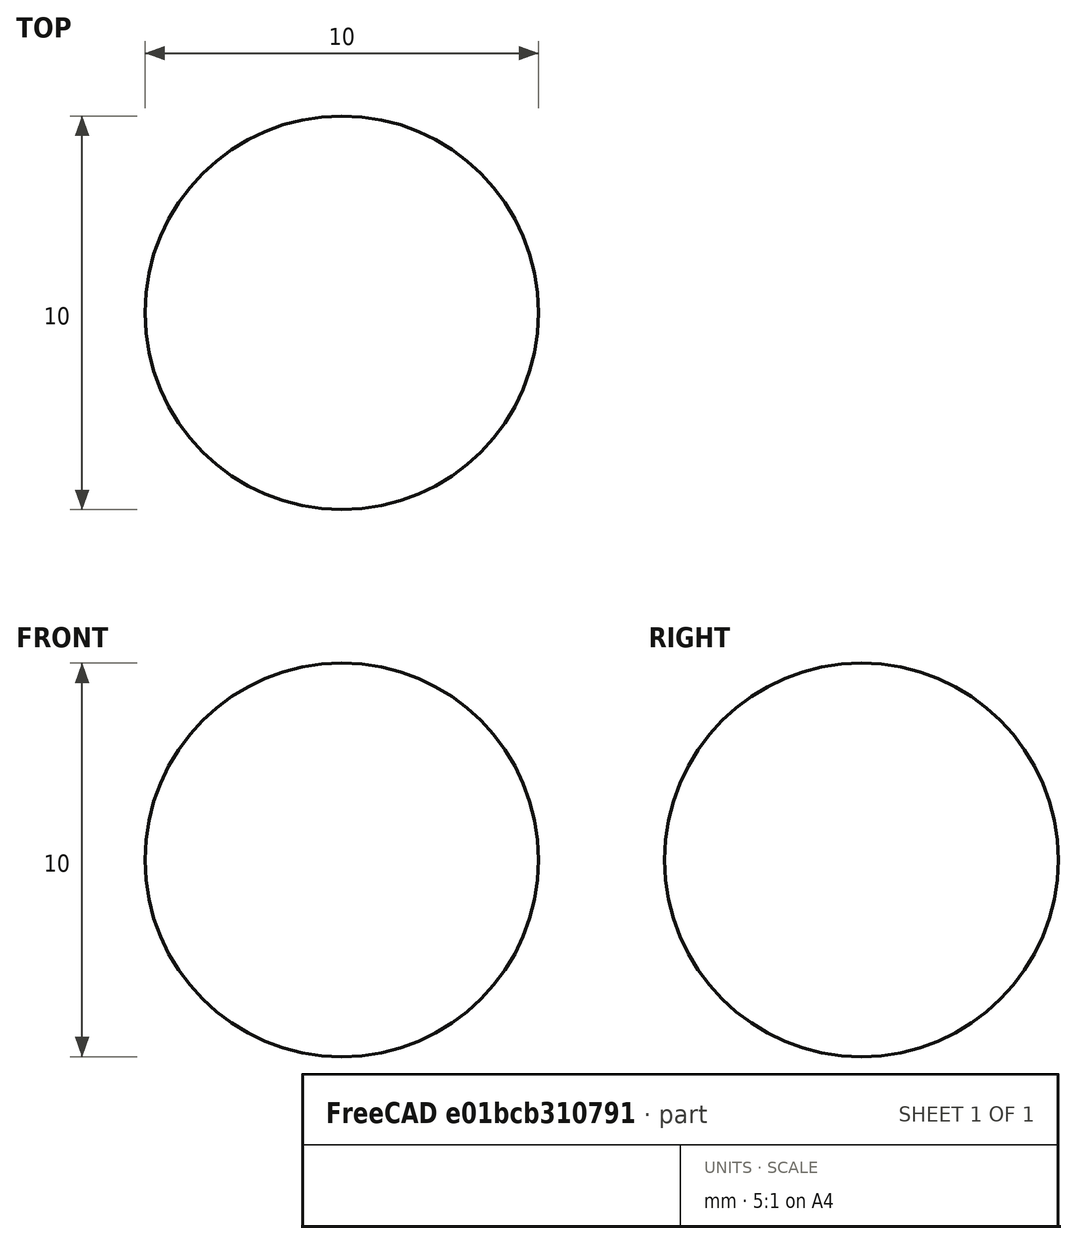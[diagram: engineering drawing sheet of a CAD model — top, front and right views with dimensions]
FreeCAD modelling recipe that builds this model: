
FCSTD DOCUMENT  (FreeCAD 0.19R17089 +1543 (Git))
Label: move
License: All rights reserved
LicenseURL: http://en.wikipedia.org/wiki/All_rights_reserved
objects: App::FeaturePython×2, Part::FeaturePython×2, Sketcher::SketchObject×1, PartDesign::Revolution×1, PartDesign::Body×1, App::DocumentObjectGroup×1
note: 5 computed .brp shape members not serialized (recipe doc carries the construction recipe); baked Part::Feature solids carry a one-line shape summary decoded from their .brp

FEATURE [Sketcher::SketchObject] Sketch
  MapMode = 5
  Support = -> [XY_Plane]
  sketch-geometry (2):
    g0: ArcOfCircle CenterX=0 CenterY=0 CenterZ=0 NormalX=0 NormalY=0 NormalZ=1 AngleXU=0 Radius=5 StartAngle=0 EndAngle=3.14159
    g1: LineSegment StartX=-5 StartY=-1.6e-15 StartZ=0 EndX=5 EndY=1e-16 EndZ=0
  constraints (6):
    c: Coincident(g0,g-1)
    c: PointOnObject(g0,g-1)
    c: PointOnObject(g0,g-1)
    c: Radius(g0) = 5  'R1'
    c: Coincident(g1,g0)
    c: Coincident(g1,g0)
FEATURE [PartDesign::Revolution] Revolution
  Angle = 360
  Axis = (1,0,0)
  Base = (0,0,0)
  ClaimChildren = false
  Profile = -> Sketch
  ReferenceAxis = -> Sketch [H_Axis]
FEATURE [PartDesign::Body] Body
  Group = -> [Sketch,Revolution]
  Origin = -> Origin
  Tip = -> Revolution
FEATURE [App::FeaturePython] Constraints  # WARN: FeaturePython — macro-defined, semantics opaque (R4)
  GroupMode = 1
  _Version = 1
FEATURE [App::FeaturePython] Elements  # WARN: FeaturePython — macro-defined, semantics opaque (R4)
  GroupMode = 1
FEATURE [Part::FeaturePython] Parts  # WARN: FeaturePython — macro-defined, semantics opaque (R4)
  Group = -> [Body]
  GroupMode = 0
FEATURE [Part::FeaturePython] Assembly  label="Sphere"  # WARN: FeaturePython — macro-defined, semantics opaque (R4)
  AutoRelax = true
  BuildShape = 0
  Freeze = false
  Group = -> [Constraints,Elements,Parts]
  GroupMode = 1
  SolverType = 1
  Verbose = false
  _SolverType = 1
  _Version = 1
FEATURE [App::DocumentObjectGroup] Group  label="Repository"
  Group = -> [Assembly]
